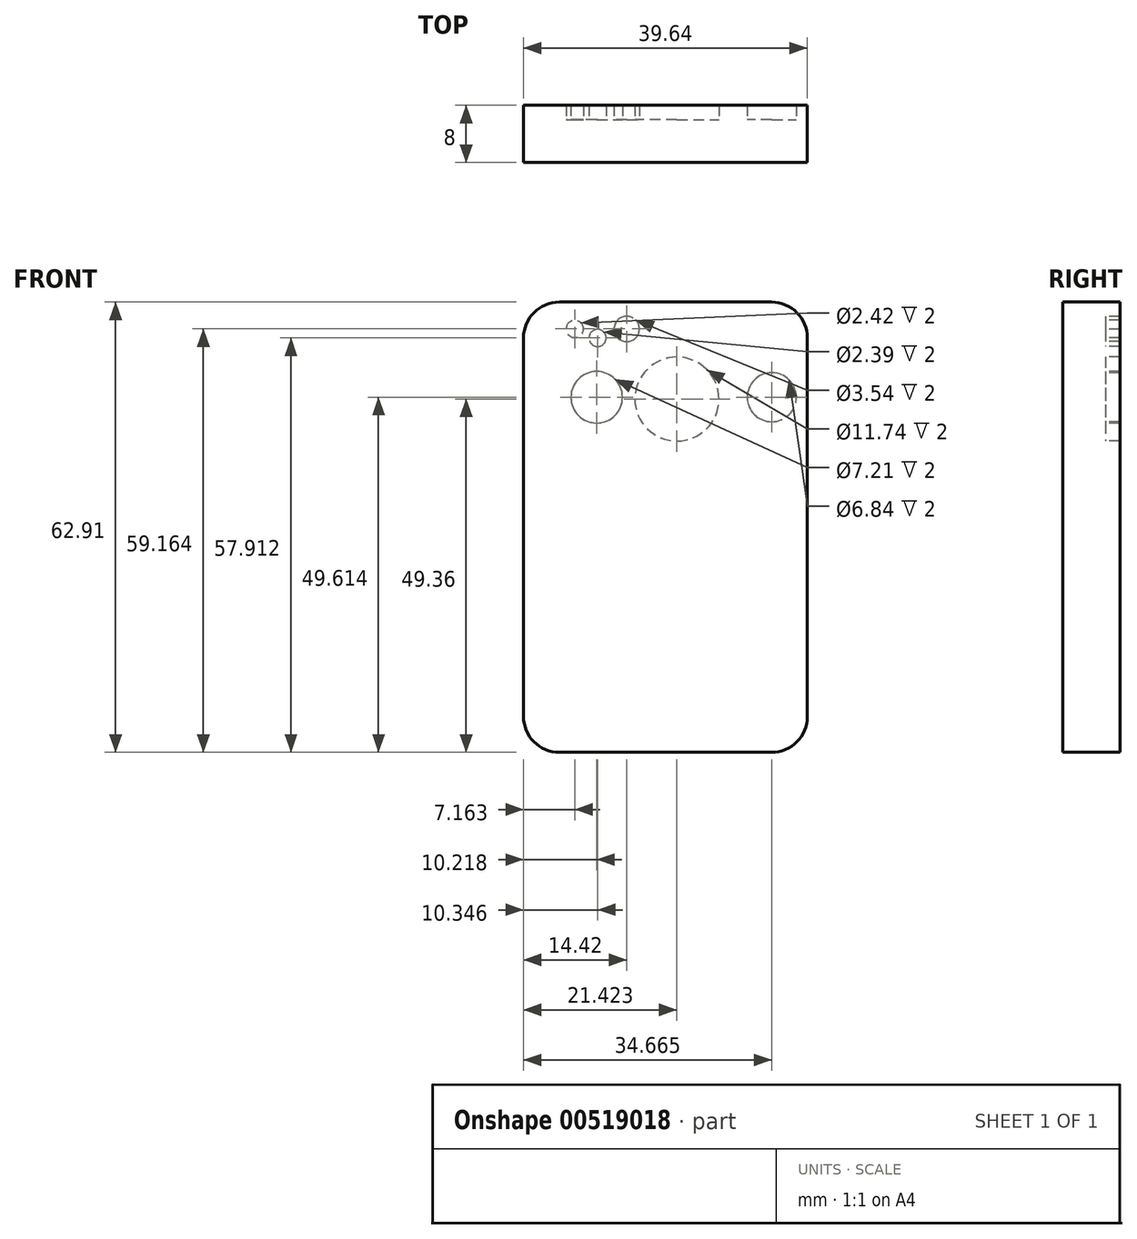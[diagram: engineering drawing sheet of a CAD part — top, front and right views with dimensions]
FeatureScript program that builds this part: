
annotation { "Feature Type Name" : "Feature", "Feature Type Description" : "" }
export const myFeature = defineFeature(function(context is Context, id is Id, definition is map)
    precondition{}
    {
        {
            var Q0;
            Q0=qCreatedBy(makeId("Front.planeOp"),FACE);
            var sketch = newSketch(context, id + "F0", { "sketchPlane" : qUnion([Q0])});
            skLineSegment(sketch, "E0.bottom", {"start": v(-45.36, 49.01) * mm, "end": v(-5.72, 49.01) * mm});
            skLineSegment(sketch, "E0.top", {"start": v(-45.36, -13.9) * mm, "end": v(-5.72, -13.9) * mm});
            skLineSegment(sketch, "E0.left", {"start": v(-45.36, 49.01) * mm, "end": v(-45.36, -13.9) * mm});
            skLineSegment(sketch, "E0.right", {"start": v(-5.72, 49.01) * mm, "end": v(-5.72, -13.9) * mm});
            skSolve(sketch);
        }
        {
            var Q0;
            Q0=makeQuery(id+"F0.imprint","IMPRINT",FACE,{"disambiguationData":[TD([[makeQuery(id+"F0.imprint","IMPRINT",EDGE,{"derivedFrom":sQuery(id+"F0.wireOp",EDGE,"E0.bottom")}),-1.0]])]});
            extrude(context, id + "F1", {"entities" : qUnion([Q0]), "depth" : 3 * mm, "offsetDistance" : 25 * mm});
        }
        {
            var Q0;
            Q0=makeQuery(id+"F1.opExtrude","SWEPT_EDGE",EDGE,{"disambiguationData":[OSD([sQuery(id+"F0.wireOp",EDGE,"E0.bottom"),sQuery(id+"F0.wireOp",EDGE,"E0.left")])]});
            var Q1;
            Q1=makeQuery(id+"F1.opExtrude","SWEPT_EDGE",EDGE,{"disambiguationData":[OSD([sQuery(id+"F0.wireOp",EDGE,"E0.top"),sQuery(id+"F0.wireOp",EDGE,"E0.left")])]});
            var Q2;
            Q2=makeQuery(id+"F1.opExtrude","SWEPT_EDGE",EDGE,{"disambiguationData":[OSD([sQuery(id+"F0.wireOp",EDGE,"E0.top"),sQuery(id+"F0.wireOp",EDGE,"E0.right")])]});
            var Q3;
            Q3=makeQuery(id+"F1.opExtrude","SWEPT_EDGE",EDGE,{"disambiguationData":[OSD([sQuery(id+"F0.wireOp",EDGE,"E0.bottom"),sQuery(id+"F0.wireOp",EDGE,"E0.right")])]});
            fillet(context, id + "F2", {"entities" : qUnion([Q0, Q1, Q2, Q3]), "radius" : 5 * mm, "tangentPropagation" : true, "allowEdgeOverflow" : false});
        }
        {
            var Q0;
            Q0=makeQuery(id+"F1.opExtrude","CAP_FACE",FACE,{"disambiguationData":[OSD([sQuery(id+"F0.wireOp",EDGE,"E0.bottom"),sQuery(id+"F0.wireOp",EDGE,"E0.top"),sQuery(id+"F0.wireOp",EDGE,"E0.left"),sQuery(id+"F0.wireOp",EDGE,"E0.right")])],"isStart":true});
            var sketch = newSketch(context, id + "F3", { "sketchPlane" : qUnion([Q0])});
            skCircle(sketch, "E1", {"center": v(38.2, 45.26) * mm, "radius": 1.2 * mm});
            skCircle(sketch, "E2", {"center": v(35.01, 44.01) * mm, "radius": 1.2 * mm});
            skCircle(sketch, "E3", {"center": v(30.94, 45.26) * mm, "radius": 1.77 * mm});
            skCircle(sketch, "E4", {"center": v(23.94, 35.46) * mm, "radius": 5.87 * mm});
            skCircle(sketch, "E5", {"center": v(35.14, 35.71) * mm, "radius": 3.6 * mm});
            skCircle(sketch, "E6", {"center": v(10.7, 35.71) * mm, "radius": 3.42 * mm});
            skSolve(sketch);
        }
        {
            var Q0;
            Q0=makeQuery(id+"F1.opExtrude","CAP_FACE",FACE,{"disambiguationData":[OSD([sQuery(id+"F0.wireOp",EDGE,"E0.bottom"),sQuery(id+"F0.wireOp",EDGE,"E0.top"),sQuery(id+"F0.wireOp",EDGE,"E0.left"),sQuery(id+"F0.wireOp",EDGE,"E0.right")])],"isStart":false});
            var sketch = newSketch(context, id + "F4", { "sketchPlane" : qUnion([Q0])});
            skSolve(sketch);
        }
        {
            var Q0;
            Q0 = qSketchRegion(id + "F3", true);
            var Q1;
            Q1=makeQuery(id+"F3.imprint","IMPRINT",FACE,{"disambiguationData":[TD([[makeQuery(id+"F3.imprint","IMPRINT",EDGE,{"derivedFrom":sQuery(id+"F3.wireOp",EDGE,"E4")}),1.0]])]});
            extrude(context, id + "F5", {"entities" : qUnion([Q0, Q1]), "operationType" : NewBodyOperationType.ADD, "depth" : 3 * mm, "offsetDistance" : 25 * mm});
        }
        {
            var Q0;
            Q0=makeQuery(id+"F1.opExtrude","CAP_FACE",FACE,{"disambiguationData":[OSD([sQuery(id+"F0.wireOp",EDGE,"E0.bottom"),sQuery(id+"F0.wireOp",EDGE,"E0.top"),sQuery(id+"F0.wireOp",EDGE,"E0.left"),sQuery(id+"F0.wireOp",EDGE,"E0.right")])],"isStart":true});
            extrude(context, id + "F6", {"entities" : qUnion([Q0]), "operationType" : NewBodyOperationType.ADD, "depth" : 5 * mm, "offsetDistance" : 25 * mm});
        }
        {
            var Q0;
            {var subQ0=sQuery(id+"F0.wireOp",EDGE,"E0.bottom");Q0=makeQuery(id+"F6.boolean.opBoolean","MERGE",FACE,{"derivedFrom":[makeQuery(id+"F1.opExtrude","SWEPT_FACE",FACE,{"disambiguationData":[OSD([subQ0])]}),makeQuery(id+"F6.opExtrude","SWEPT_FACE",FACE,{"disambiguationData":[OSD([subQ0])]})]});}
            var sketch = newSketch(context, id + "F7", { "sketchPlane" : qUnion([Q0])});
            skCircle(sketch, "E7", {"center": v(-20.2, 5) * mm, "radius": 4.05 * mm});
            skSolve(sketch);
        }
        {
            var Q0;
            {var subQ3=sQuery(id+"F0.wireOp",EDGE,"E0.bottom");Q0=makeQuery(id+"F7.imprint","IMPRINT",FACE,{"disambiguationData":[TD([[makeQuery(id+"F7.imprint","IMPRINT",EDGE,{"derivedFrom":makeQuery(id+"F1.opExtrude","CAP_EDGE",EDGE,{"disambiguationData":[OSD([subQ3])],"isStart":false})}),1.0]])]});}
            var sketch = newSketch(context, id + "F8", { "sketchPlane" : qUnion([Q0])});
            skCircle(sketch, "E8", {"center": v(-34.35, 0) * mm, "radius": 2.41 * mm});
            skSolve(sketch);
        }
        {
            var Q0;
            Q0=sQuery(id+"F8.wireOp",EDGE,"E8");
            extrude(context, id + "F9", {"bodyType" : ToolBodyType.SURFACE, "surfaceEntities" : qUnion([Q0]), "depth" : -5 * mm, "offsetDistance" : 25 * mm});
        }
    });
